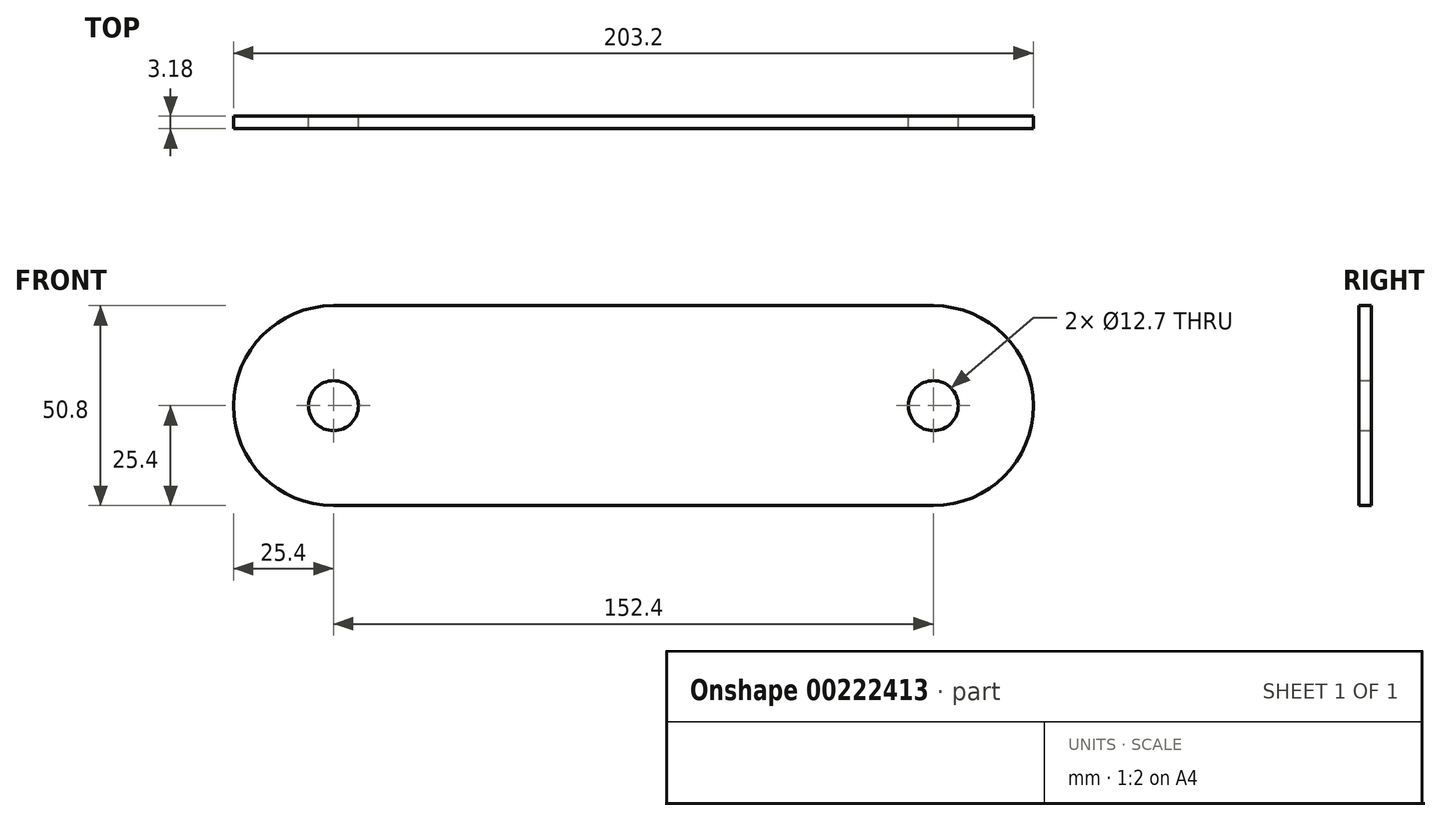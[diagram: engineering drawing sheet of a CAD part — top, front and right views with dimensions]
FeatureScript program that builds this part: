
annotation { "Feature Type Name" : "Feature", "Feature Type Description" : "" }
export const myFeature = defineFeature(function(context is Context, id is Id, definition is map)
    precondition{}
    {
        {
            var Q0;
            Q0=qCreatedBy(makeId("Front.planeOp"),FACE);
            var sketch = newSketch(context, id + "F0", { "sketchPlane" : qUnion([Q0])});
            skCircle(sketch, "E0", {"center": v(0, 0) * mm, "radius": 6.35 * mm});
            skCircle(sketch, "E1", {"center": v(152.4, 0) * mm, "radius": 6.35 * mm});
            skArc(sketch, "E2", {"start": v(0, -25.4) * mm, "mid": v(-25.4, 0) * mm, "end": v(0, 25.4) * mm});
            skArc(sketch, "E3", {"start": v(152.4, -25.4) * mm, "mid": v(177.8, 0) * mm, "end": v(152.4, 25.4) * mm});
            skLineSegment(sketch, "E4", {"start": v(0, 25.4) * mm, "end": v(152.4, 25.4) * mm});
            skLineSegment(sketch, "E5", {"start": v(152.4, -25.4) * mm, "end": v(0, -25.4) * mm});
            skSolve(sketch);
        }
        {
            var Q0;
            Q0=makeQuery(id+"F0.imprint","IMPRINT",FACE,{"disambiguationData":[TD([[makeQuery(id+"F0.imprint","IMPRINT",EDGE,{"derivedFrom":sQuery(id+"F0.wireOp",EDGE,"E0")}),-1.0]])]});
            extrude(context, id + "F1", {"entities" : qUnion([Q0]), "depth" : 3.17 * mm});
        }
    });
